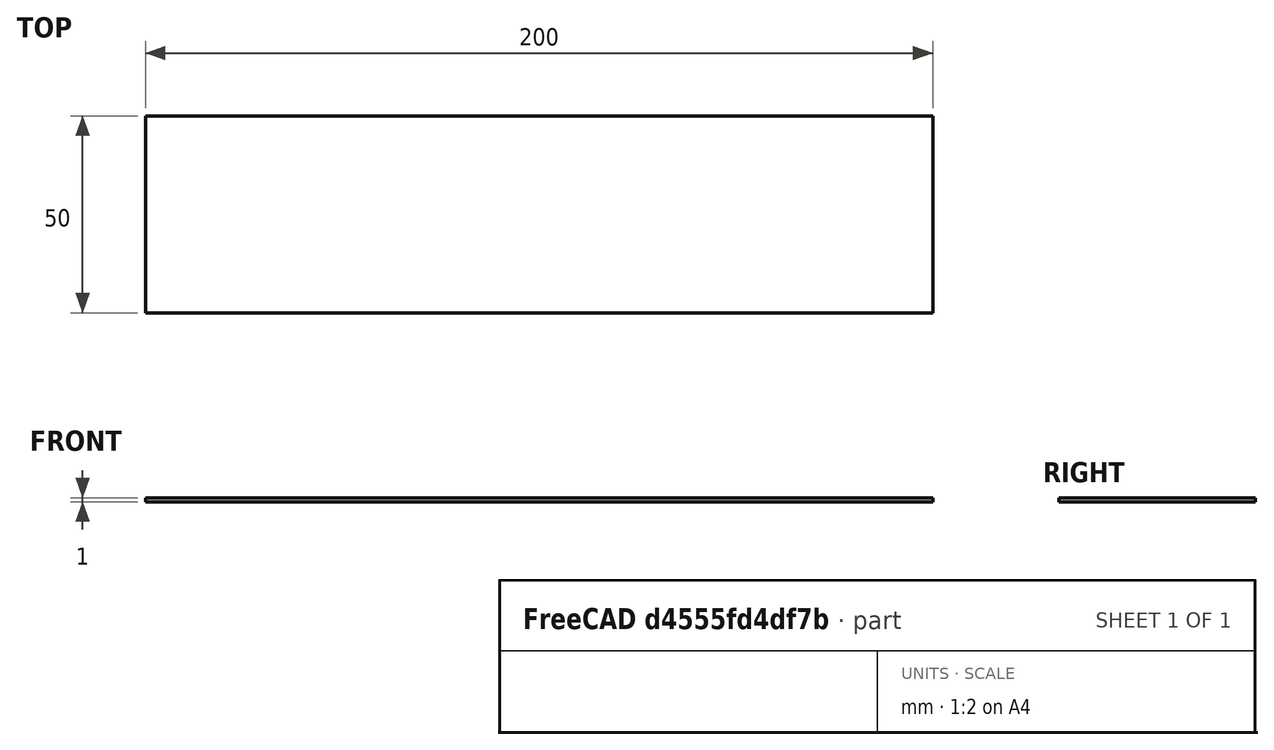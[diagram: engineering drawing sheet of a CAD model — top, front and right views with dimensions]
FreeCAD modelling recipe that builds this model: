
FCSTD DOCUMENT
Label: ledicator
objects: Sketcher::SketchObject×2, Part::Extrusion×1, PartDesign::Pad×1
note: 5 computed .brp shape members not serialized (recipe doc carries the construction recipe); baked Part::Feature solids carry a one-line shape summary decoded from their .brp

FEATURE [Sketcher::SketchObject] Sketch
  sketch-geometry (26):
    g0: LineSegment StartX=200 StartY=-50 StartZ=0 EndX=0 EndY=-50 EndZ=0
    g1: LineSegment StartX=0 StartY=-50 StartZ=0 EndX=0 EndY=-25 EndZ=0
    g2: LineSegment StartX=0 StartY=-25 StartZ=0 EndX=200 EndY=-25 EndZ=0
    g3: LineSegment StartX=200 StartY=-25 StartZ=0 EndX=200 EndY=-50 EndZ=0
    g4: LineSegment StartX=0 StartY=-25 StartZ=0 EndX=0 EndY=0 EndZ=0
    g5: LineSegment StartX=0 StartY=0 StartZ=0 EndX=200 EndY=0 EndZ=0
    g6: LineSegment StartX=200 StartY=-25 StartZ=0 EndX=200 EndY=0 EndZ=0
    g7: LineSegment StartX=40 StartY=-25 StartZ=0 EndX=40 EndY=0 EndZ=0
    g8: LineSegment StartX=70 StartY=0 StartZ=0 EndX=70 EndY=-25 EndZ=0
    g9: LineSegment StartX=90 StartY=0 StartZ=0 EndX=90 EndY=-25 EndZ=0
    g10: LineSegment StartX=120 StartY=0 StartZ=0 EndX=120 EndY=-25 EndZ=0
    g11: LineSegment StartX=100 StartY=0 StartZ=0 EndX=100 EndY=-25 EndZ=0
    g12: LineSegment StartX=150 StartY=0 StartZ=0 EndX=150 EndY=-25 EndZ=0
    g13: LineSegment StartX=190 StartY=0 StartZ=0 EndX=190 EndY=-25 EndZ=0
    g14: LineSegment StartX=80 StartY=0 StartZ=0 EndX=80 EndY=-25 EndZ=0
    g15: LineSegment StartX=110 StartY=0 StartZ=0 EndX=110 EndY=-25 EndZ=0
    g16: LineSegment StartX=130 StartY=-25 StartZ=0 EndX=130 EndY=0 EndZ=0
    g17: LineSegment StartX=20 StartY=0 StartZ=0 EndX=20 EndY=-25 EndZ=0
    g18: LineSegment StartX=30 StartY=0 StartZ=0 EndX=30 EndY=-25 EndZ=0
    g19: LineSegment StartX=50 StartY=0 StartZ=0 EndX=50 EndY=-25 EndZ=0
    g20: LineSegment StartX=10 StartY=-25 StartZ=0 EndX=10 EndY=0 EndZ=0
    g21: LineSegment StartX=170 StartY=0 StartZ=0 EndX=170 EndY=-25 EndZ=0
    g22: LineSegment StartX=140 StartY=0 StartZ=0 EndX=140 EndY=-25 EndZ=0
    g23: LineSegment StartX=60 StartY=0 StartZ=0 EndX=60 EndY=-25 EndZ=0
    g24: LineSegment StartX=160 StartY=0 StartZ=0 EndX=160 EndY=-25 EndZ=0
    g25: LineSegment StartX=180 StartY=0 StartZ=0 EndX=180 EndY=-25 EndZ=0
  constraints (96):
    c: Coincident(g0,g1)
    c: Coincident(g1,g2)
    c: Coincident(g2,g3)
    c: Coincident(g3,g0)
    c: Horizontal(g0)
    c: Horizontal(g2)
    c: Vertical(g1)
    c: Vertical(g3)
    c: Coincident(g4,g1)
    c: Vertical(g4)
    c: Horizontal(g5)
    c: Vertical(g6)
    c: Coincident(g6,g2)
    c: Coincident(g5,g4)
    c: Distance(g5) = 200
    c: Distance(g4) = 25
    c: Distance(g4,g0) = 50
    c: Coincident(g6,g5)
    c: Vertical(g7)
    c: Vertical(g10)
    c: Vertical(g11)
    c: Vertical(g12)
    c: Vertical(g17)
    c: Vertical(g25)
    c: Vertical(g18)
    c: Vertical(g20)
    c: Vertical(g19)
    c: Vertical(g13)
    c: Vertical(g23)
    c: Vertical(g8)
    c: Vertical(g14)
    c: Vertical(g9)
    c: Vertical(g15)
    c: Vertical(g16)
    c: Vertical(g22)
    c: Vertical(g21)
    c: Vertical(g24)
    c: Equal(g20,g17)
    c: Equal(g17,g18)
    c: Equal(g18,g19)
    c: Equal(g19,g7)
    c: Equal(g7,g13)
    c: Equal(g13,g23)
    c: Equal(g23,g8)
    c: Equal(g8,g14)
    c: Equal(g14,g9)
    c: Equal(g9,g11)
    c: Equal(g11,g15)
    c: Equal(g15,g10)
    c: Equal(g10,g22)
    c: Equal(g22,g16)
    c: Equal(g16,g24)
    c: Equal(g24,g12)
    c: Equal(g12,g21)
    c: Equal(g21,g25)
    c: DistanceX(g17,g20) = -10
    c: DistanceX(g18,g17) = -10
    c: DistanceX(g7,g18) = -10
    c: DistanceX(g19,g7) = -10
    c: DistanceX(g23,g19) = -10
    c: DistanceX(g8,g23) = -10
    c: DistanceX(g14,g8) = -10
    c: DistanceX(g14,g9) = 10
    c: DistanceX(g11,g9) = -10
    c: DistanceX(g11,g15) = 10
    c: DistanceX(g10,g15) = -10
    c: DistanceX(g16,g10) = -10
    c: DistanceX(g22,g16) = -10
    c: DistanceX(g12,g22) = -10
    c: DistanceX(g24,g12) = -10
    c: DistanceX(g21,g24) = -10
    c: DistanceX(g25,g21) = -10
    c: DistanceX(g13,g25) = -10
    c: DistanceX(g13,g5) = 10
    c: PointOnObject(g21,g5)
    c: PointOnObject(g24,g5)
    c: PointOnObject(g13,g5)
    c: PointOnObject(g12,g5)
    c: PointOnObject(g22,g5)
    c: PointOnObject(g16,g5)
    c: PointOnObject(g10,g5)
    c: PointOnObject(g15,g5)
    c: PointOnObject(g11,g5)
    c: PointOnObject(g9,g5)
    c: PointOnObject(g14,g5)
    c: PointOnObject(g8,g5)
    c: PointOnObject(g23,g5)
    c: PointOnObject(g7,g5)
    c: PointOnObject(g19,g5)
    c: PointOnObject(g18,g5)
    c: PointOnObject(g17,g5)
    c: PointOnObject(g20,g5)
    c: PointOnObject(g25,g5)
    c: PointOnObject(g13,g2)
    c: DistanceX(g4) = 0
    c: DistanceY(g4) = 0
FEATURE [Part::Extrusion] Extrude
  Base = -> Sketch
  Dir = (0,0,25)
FEATURE [Sketcher::SketchObject] Sketch002
  sketch-geometry (4):
    g0: LineSegment StartX=0 StartY=-50 StartZ=0 EndX=200 EndY=-50 EndZ=0
    g1: LineSegment StartX=200 StartY=-50 StartZ=0 EndX=200 EndY=0 EndZ=0
    g2: LineSegment StartX=200 StartY=0 StartZ=0 EndX=0 EndY=0 EndZ=0
    g3: LineSegment StartX=0 StartY=0 StartZ=0 EndX=0 EndY=-50 EndZ=0
  constraints (12):
    c: Coincident(g0,g1)
    c: Coincident(g1,g2)
    c: Coincident(g2,g3)
    c: Coincident(g3,g0)
    c: Horizontal(g0)
    c: Horizontal(g2)
    c: Vertical(g1)
    c: Vertical(g3)
    c: DistanceX(g2) = -200
    c: DistanceY(g3) = -50
    c: DistanceX(g2) = 0
    c: DistanceY(g2) = 0
FEATURE [PartDesign::Pad] Pad
  Length = 1
  MirroredExtent = false
  Reversed = true
  Sketch = -> Sketch002
